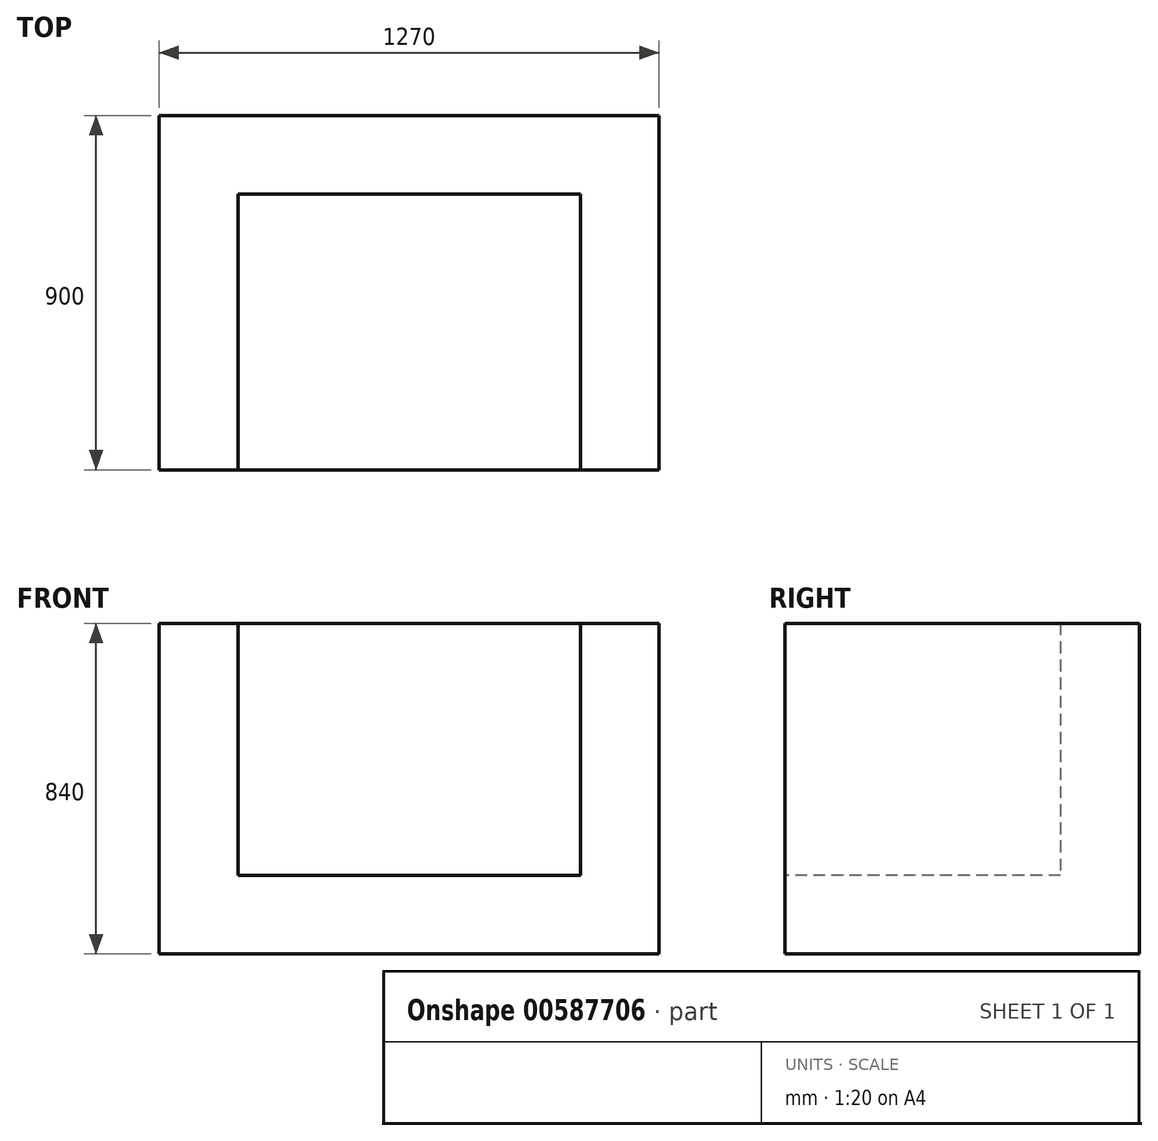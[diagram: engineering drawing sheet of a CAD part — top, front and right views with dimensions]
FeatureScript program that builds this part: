
annotation { "Feature Type Name" : "Feature", "Feature Type Description" : "" }
export const myFeature = defineFeature(function(context is Context, id is Id, definition is map)
    precondition{}
    {
        {
            var Q0;
            Q0=qCreatedBy(makeId("Top.planeOp"),FACE);
            var sketch = newSketch(context, id + "F0", { "sketchPlane" : qUnion([Q0])});
            skLineSegment(sketch, "E0.bottom", {"start": v(-668.62, 360.38) * mm, "end": v(601.38, 360.38) * mm});
            skLineSegment(sketch, "E0.top", {"start": v(-668.62, -539.62) * mm, "end": v(601.38, -539.62) * mm});
            skLineSegment(sketch, "E0.left", {"start": v(-668.62, 360.38) * mm, "end": v(-668.62, -539.62) * mm});
            skLineSegment(sketch, "E0.right", {"start": v(601.38, 360.38) * mm, "end": v(601.38, -539.62) * mm});
            skSolve(sketch);
        }
        {
            var Q0;
            Q0=makeQuery(id+"F0.imprint","IMPRINT",FACE,{"disambiguationData":[TD([[makeQuery(id+"F0.imprint","IMPRINT",EDGE,{"derivedFrom":sQuery(id+"F0.wireOp",EDGE,"E0.bottom")}),-1.0]])]});
            extrude(context, id + "F1", {"entities" : qUnion([Q0]), "depth" : 840 * mm, "offsetDistance" : 25 * mm});
        }
        {
            var Q0;
            Q0=makeQuery(id+"F1.opExtrude","CAP_FACE",FACE,{"disambiguationData":[OSD([sQuery(id+"F0.wireOp",EDGE,"E0.bottom"),sQuery(id+"F0.wireOp",EDGE,"E0.top"),sQuery(id+"F0.wireOp",EDGE,"E0.left"),sQuery(id+"F0.wireOp",EDGE,"E0.right")])],"isStart":false});
            var Q1;
            Q1=makeQuery(id+"F1.opExtrude","SWEPT_FACE",FACE,{"disambiguationData":[OSD([sQuery(id+"F0.wireOp",EDGE,"E0.top")])]});
            shell(context, id + "F2", {"entities" : qUnion([Q0, Q1]), "thickness" : 200 * mm});
        }
    });
